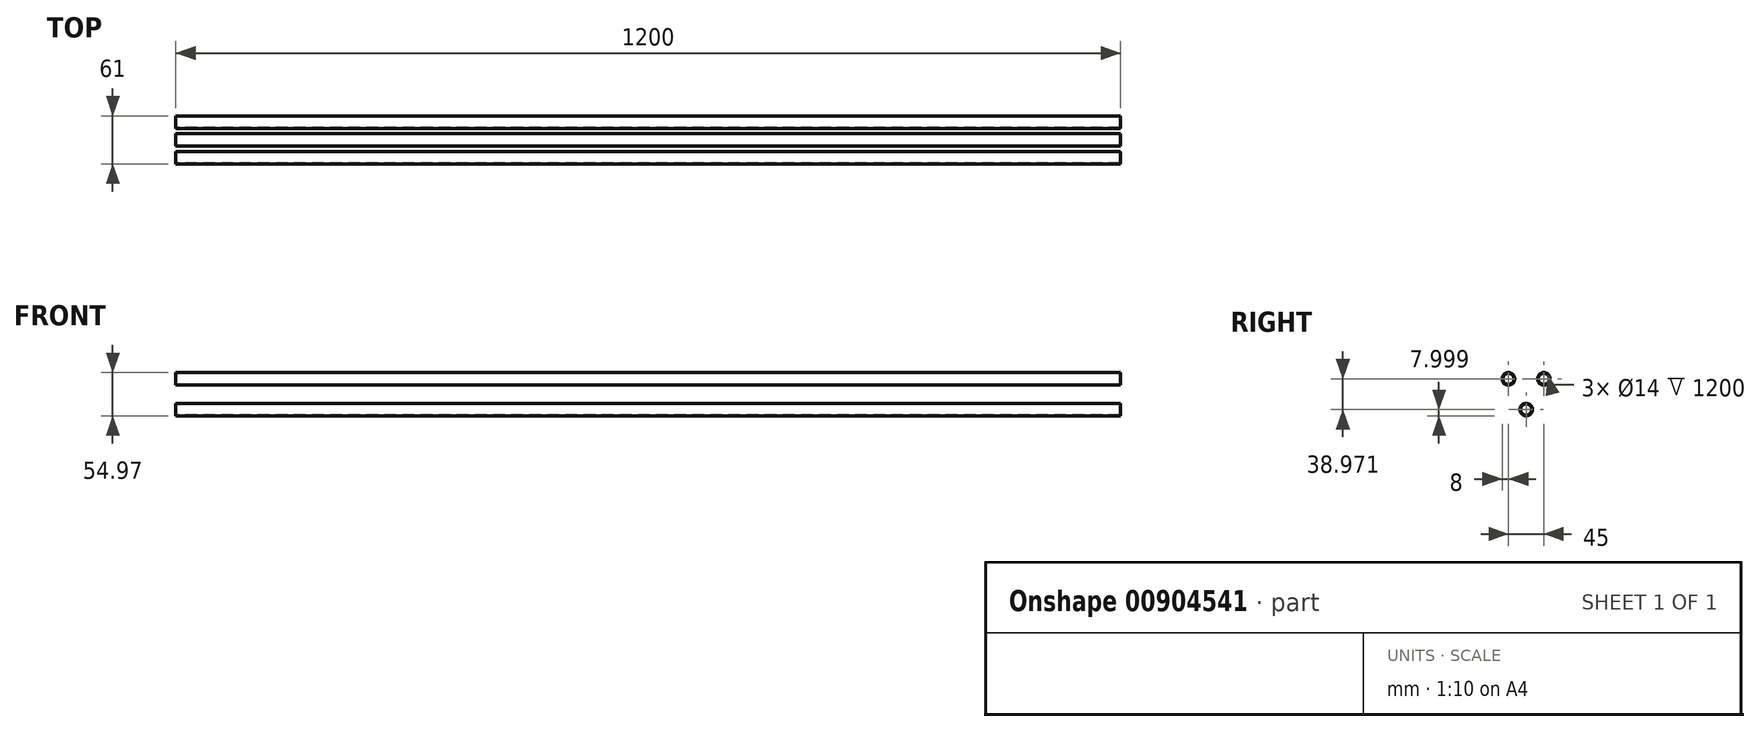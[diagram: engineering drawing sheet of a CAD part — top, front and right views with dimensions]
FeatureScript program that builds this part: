
annotation { "Feature Type Name" : "Feature", "Feature Type Description" : "" }
export const myFeature = defineFeature(function(context is Context, id is Id, definition is map)
    precondition{}
    {
        {
            var Q0;
            Q0=qCreatedBy(makeId("Right.planeOp"),FACE);
            var sketch = newSketch(context, id + "F0", { "sketchPlane" : qUnion([Q0])});
            skCircle(sketch, "E0", {"center": v(0, 0) * mm, "radius": 8 * mm});
            skCircle(sketch, "E1", {"center": v(45, 0) * mm, "radius": 8 * mm});
            skCircle(sketch, "E2", {"center": v(22.5, -38.97) * mm, "radius": 8 * mm});
            skCircle(sketch, "E3", {"center": v(0, 0) * mm, "radius": 7 * mm});
            skCircle(sketch, "E4", {"center": v(45, 0) * mm, "radius": 7 * mm});
            skCircle(sketch, "E5", {"center": v(22.5, -38.97) * mm, "radius": 7 * mm});
            skSolve(sketch);
        }
        {
            var Q0;
            Q0=makeQuery(id+"F0.imprint","IMPRINT",FACE,{"disambiguationData":[TD([[makeQuery(id+"F0.imprint","IMPRINT",EDGE,{"derivedFrom":sQuery(id+"F0.wireOp",EDGE,"E0")}),1.0]])]});
            var Q1;
            Q1=makeQuery(id+"F0.imprint","IMPRINT",FACE,{"disambiguationData":[TD([[makeQuery(id+"F0.imprint","IMPRINT",EDGE,{"derivedFrom":sQuery(id+"F0.wireOp",EDGE,"E1")}),1.0]])]});
            var Q2;
            Q2=makeQuery(id+"F0.imprint","IMPRINT",FACE,{"disambiguationData":[TD([[makeQuery(id+"F0.imprint","IMPRINT",EDGE,{"derivedFrom":sQuery(id+"F0.wireOp",EDGE,"E2")}),1.0]])]});
            extrude(context, id + "F1", {"entities" : qUnion([Q0, Q1, Q2]), "depth" : 1200 * mm, "offsetDistance" : 25 * mm});
        }
    });
